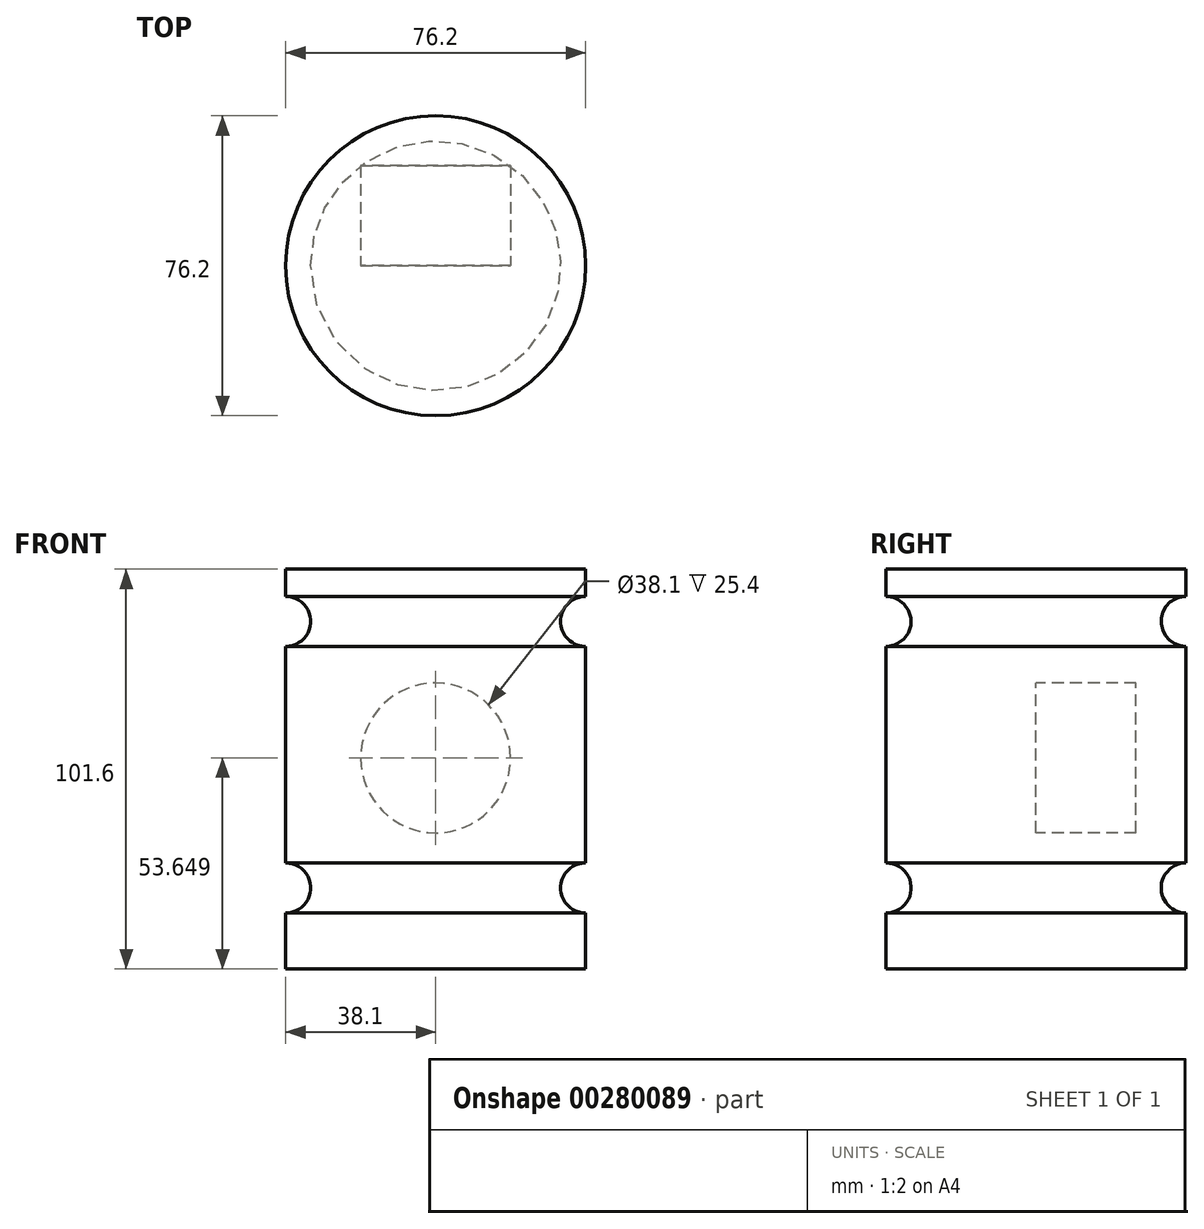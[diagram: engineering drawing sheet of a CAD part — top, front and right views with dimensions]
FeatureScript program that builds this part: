
annotation { "Feature Type Name" : "Feature", "Feature Type Description" : "" }
export const myFeature = defineFeature(function(context is Context, id is Id, definition is map)
    precondition{}
    {
        {
            var Q0;
            Q0=qCreatedBy(makeId("Front.planeOp"),FACE);
            var sketch = newSketch(context, id + "F0", { "sketchPlane" : qUnion([Q0])});
            skLineSegment(sketch, "E0.bottom", {"start": v(0, 0) * mm, "end": v(-38.1, 0) * mm});
            skLineSegment(sketch, "E0.top", {"start": v(0, 101.6) * mm, "end": v(-38.1, 101.6) * mm});
            skLineSegment(sketch, "E0.left", {"start": v(0, 0) * mm, "end": v(0, 101.6) * mm});
            skLineSegment(sketch, "E0.right", {"start": v(-38.1, 0) * mm, "end": v(-38.1, 14.26) * mm});
            skArc(sketch, "E1", {"start": v(-38.1, 82) * mm, "mid": v(-31.75, 88.34) * mm, "end": v(-38.1, 94.7) * mm});
            skArc(sketch, "E2", {"start": v(-38.1, 14.26) * mm, "mid": v(-31.75, 20.6) * mm, "end": v(-38.1, 26.96) * mm});
            skLineSegment(sketch, "E3.trimOffspring", {"start": v(-38.1, 94.7) * mm, "end": v(-38.1, 101.6) * mm});
            skLineSegment(sketch, "E4.trimOffspring", {"start": v(-38.1, 26.96) * mm, "end": v(-38.1, 82) * mm});
            skSolve(sketch);
        }
        {
            var Q0;
            Q0=makeQuery(id+"F0.imprint","IMPRINT",FACE,{"disambiguationData":[TD([[makeQuery(id+"F0.imprint","IMPRINT",EDGE,{"derivedFrom":sQuery(id+"F0.wireOp",EDGE,"E0.bottom")}),-1.0]])]});
            var Q1;
            Q1=sQuery(id+"F0.wireOp",EDGE,"E0.left");
            revolve(context, id + "F1", {"entities" : qUnion([Q0]), "axis" : qUnion([Q1]), "revolveType" : RevolveType.FULL});
        }
        {
            var Q0;
            Q0=qCreatedBy(makeId("Front.planeOp"),FACE);
            var sketch = newSketch(context, id + "F2", { "sketchPlane" : qUnion([Q0])});
            skCircle(sketch, "E5", {"center": v(0, 53.65) * mm, "radius": 19.05 * mm});
            skSolve(sketch);
        }
        {
            var Q0;
            Q0 = qSketchRegion(id + "F2", true);
            extrude(context, id + "F3", {"entities" : qUnion([Q0]), "operationType" : NewBodyOperationType.REMOVE, "oppositeDirection" : true, "depth" : 25.4 * mm});
        }
    });
